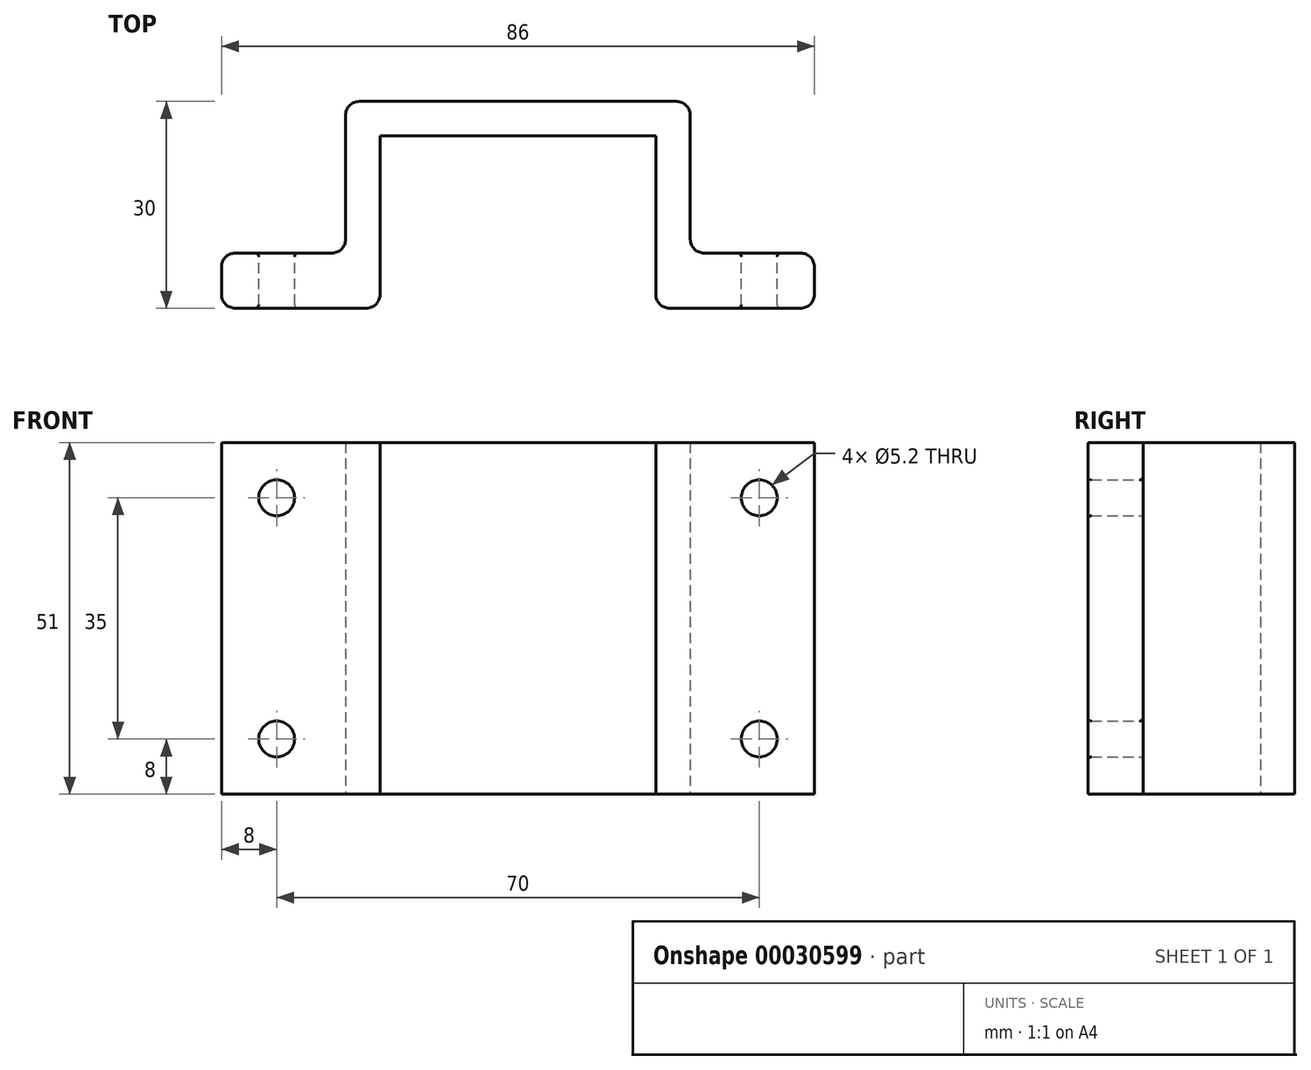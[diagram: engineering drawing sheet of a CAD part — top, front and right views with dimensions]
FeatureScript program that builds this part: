
annotation { "Feature Type Name" : "Feature", "Feature Type Description" : "" }
export const myFeature = defineFeature(function(context is Context, id is Id, definition is map)
    precondition{}
    {
        {
            var Q0;
            Q0=qCreatedBy(makeId("Top.planeOp"),FACE);
            var sketch = newSketch(context, id + "F0", { "sketchPlane" : qUnion([Q0])});
            skLineSegment(sketch, "E0", {"start": v(-20, 0) * mm, "end": v(-20, 25) * mm});
            skLineSegment(sketch, "E1", {"start": v(-20, 25) * mm, "end": v(0, 25) * mm});
            skLineSegment(sketch, "E2", {"start": v(-20, 0) * mm, "end": v(-43, 0) * mm});
            skLineSegment(sketch, "E3", {"start": v(-43, 0) * mm, "end": v(-43, 8) * mm});
            skLineSegment(sketch, "E4", {"start": v(-43, 8) * mm, "end": v(-25, 8) * mm});
            skLineSegment(sketch, "E5", {"start": v(-25, 8) * mm, "end": v(-25, 30) * mm});
            skLineSegment(sketch, "E6", {"start": v(-25, 30) * mm, "end": v(0, 30) * mm});
            skLineSegment(sketch, "E7.MirrorCS", {"start": v(20, 0) * mm, "end": v(20, 25) * mm});
            skLineSegment(sketch, "E8.MirrorCS", {"start": v(20, 25) * mm, "end": v(0, 25) * mm});
            skLineSegment(sketch, "E9.MirrorCS", {"start": v(25, 30) * mm, "end": v(0, 30) * mm});
            skLineSegment(sketch, "E10.MirrorCS", {"start": v(20, 0) * mm, "end": v(43, 0) * mm});
            skLineSegment(sketch, "E11.MirrorCS", {"start": v(43, 0) * mm, "end": v(43, 8) * mm});
            skLineSegment(sketch, "E12.MirrorCS", {"start": v(43, 8) * mm, "end": v(25, 8) * mm});
            skLineSegment(sketch, "E13.MirrorCS", {"start": v(25, 8) * mm, "end": v(25, 30) * mm});
            skSolve(sketch);
        }
        {
            var Q0;
            Q0=makeQuery(id+"F0.imprint","IMPRINT",FACE,{"disambiguationData":[TD([[makeQuery(id+"F0.imprint","IMPRINT",EDGE,{"derivedFrom":sQuery(id+"F0.wireOp",EDGE,"E0")}),1.0]])]});
            extrude(context, id + "F1", {"entities" : qUnion([Q0]), "depth" : 51 * mm});
        }
        {
            var Q0;
            Q0=makeQuery(id+"F1.opExtrude","SWEPT_FACE",FACE,{"disambiguationData":[OSD([sQuery(id+"F0.wireOp",EDGE,"E4")])]});
            var sketch = newSketch(context, id + "F2", { "sketchPlane" : qUnion([Q0])});
            skCircle(sketch, "E14", {"center": v(35, 8) * mm, "radius": 2.6 * mm});
            skCircle(sketch, "E15", {"center": v(35, 43) * mm, "radius": 2.6 * mm});
            skCircle(sketch, "E16", {"center": v(-35, 8) * mm, "radius": 2.6 * mm});
            skCircle(sketch, "E17", {"center": v(-35, 43) * mm, "radius": 2.6 * mm});
            skSolve(sketch);
        }
        {
            var Q0;
            Q0=makeQuery(id+"F1.opExtrude","SWEPT_EDGE",EDGE,{"disambiguationData":[OSD([sQuery(id+"F0.wireOp",EDGE,"E4"),sQuery(id+"F0.wireOp",EDGE,"E5")])]});
            var Q1;
            Q1=makeQuery(id+"F1.opExtrude","SWEPT_EDGE",EDGE,{"disambiguationData":[OSD([sQuery(id+"F0.wireOp",EDGE,"E12.MirrorCS"),sQuery(id+"F0.wireOp",EDGE,"E13.MirrorCS")])]});
            var Q2;
            Q2=makeQuery(id+"F1.opExtrude","SWEPT_EDGE",EDGE,{"disambiguationData":[OSD([sQuery(id+"F0.wireOp",EDGE,"E11.MirrorCS"),sQuery(id+"F0.wireOp",EDGE,"E12.MirrorCS")])]});
            var Q3;
            Q3=makeQuery(id+"F1.opExtrude","SWEPT_EDGE",EDGE,{"disambiguationData":[OSD([sQuery(id+"F0.wireOp",EDGE,"E10.MirrorCS"),sQuery(id+"F0.wireOp",EDGE,"E11.MirrorCS")])]});
            var Q4;
            Q4=makeQuery(id+"F1.opExtrude","SWEPT_EDGE",EDGE,{"disambiguationData":[OSD([sQuery(id+"F0.wireOp",EDGE,"E3"),sQuery(id+"F0.wireOp",EDGE,"E4")])]});
            var Q5;
            Q5=makeQuery(id+"F1.opExtrude","SWEPT_EDGE",EDGE,{"disambiguationData":[OSD([sQuery(id+"F0.wireOp",EDGE,"E2"),sQuery(id+"F0.wireOp",EDGE,"E3")])]});
            var Q6;
            Q6=makeQuery(id+"F1.opExtrude","SWEPT_EDGE",EDGE,{"disambiguationData":[OSD([sQuery(id+"F0.wireOp",EDGE,"E0"),sQuery(id+"F0.wireOp",EDGE,"E2")])]});
            var Q7;
            Q7=makeQuery(id+"F1.opExtrude","SWEPT_EDGE",EDGE,{"disambiguationData":[OSD([sQuery(id+"F0.wireOp",EDGE,"E7.MirrorCS"),sQuery(id+"F0.wireOp",EDGE,"E10.MirrorCS")])]});
            var Q8;
            Q8=makeQuery(id+"F1.opExtrude","SWEPT_EDGE",EDGE,{"disambiguationData":[OSD([sQuery(id+"F0.wireOp",EDGE,"E5"),sQuery(id+"F0.wireOp",EDGE,"E6")])]});
            var Q9;
            Q9=makeQuery(id+"F1.opExtrude","SWEPT_EDGE",EDGE,{"disambiguationData":[OSD([sQuery(id+"F0.wireOp",EDGE,"E9.MirrorCS"),sQuery(id+"F0.wireOp",EDGE,"E13.MirrorCS")])]});
            fillet(context, id + "F3", {"entities" : qUnion([Q0, Q1, Q2, Q3, Q4, Q5, Q6, Q7, Q8, Q9]), "radius" : 2 * mm, "tangentPropagation" : true, "allowEdgeOverflow" : false});
        }
        {
            var Q0;
            Q0=qSketchRegion(id+"F2",true);
            var Q1;
            Q1=makeQuery(id+"F1.opExtrude","SWEPT_FACE",FACE,{"disambiguationData":[OSD([sQuery(id+"F0.wireOp",EDGE,"E2")])]});
            extrude(context, id + "F4", {"entities" : qUnion([Q0]), "operationType" : NewBodyOperationType.REMOVE, "endBound" : BoundingType.UP_TO_SURFACE, "oppositeDirection" : true, "endBoundEntityFace" : qUnion([Q1]), "depth" : 25 * mm});
        }
        {
            var Q0;
            Q0=makeQuery(id+"F4.boolean.opBoolean","COPY",FACE,{"derivedFrom":makeQuery(id+"F4.opExtrude","SWEPT_FACE",FACE,{"disambiguationData":[OSD([sQuery(id+"F2.wireOp",EDGE,"E15")])]})});
            var Q1;
            Q1=makeQuery(id+"F4.boolean.opBoolean","COPY",FACE,{"derivedFrom":makeQuery(id+"F4.opExtrude","SWEPT_FACE",FACE,{"disambiguationData":[OSD([sQuery(id+"F2.wireOp",EDGE,"E14")])]})});
            var Q2;
            Q2=makeQuery(id+"F4.boolean.opBoolean","COPY",FACE,{"derivedFrom":makeQuery(id+"F4.opExtrude","SWEPT_FACE",FACE,{"disambiguationData":[OSD([sQuery(id+"F2.wireOp",EDGE,"E16")])]})});
            var Q3;
            Q3=makeQuery(id+"F4.boolean.opBoolean","COPY",FACE,{"derivedFrom":makeQuery(id+"F4.opExtrude","SWEPT_FACE",FACE,{"disambiguationData":[OSD([sQuery(id+"F2.wireOp",EDGE,"E17")])]})});
            fillet(context, id + "F5", {"entities" : qUnion([Q0, Q1, Q2, Q3]), "radius" : 0.5 * mm, "tangentPropagation" : true, "allowEdgeOverflow" : false});
        }
    });
